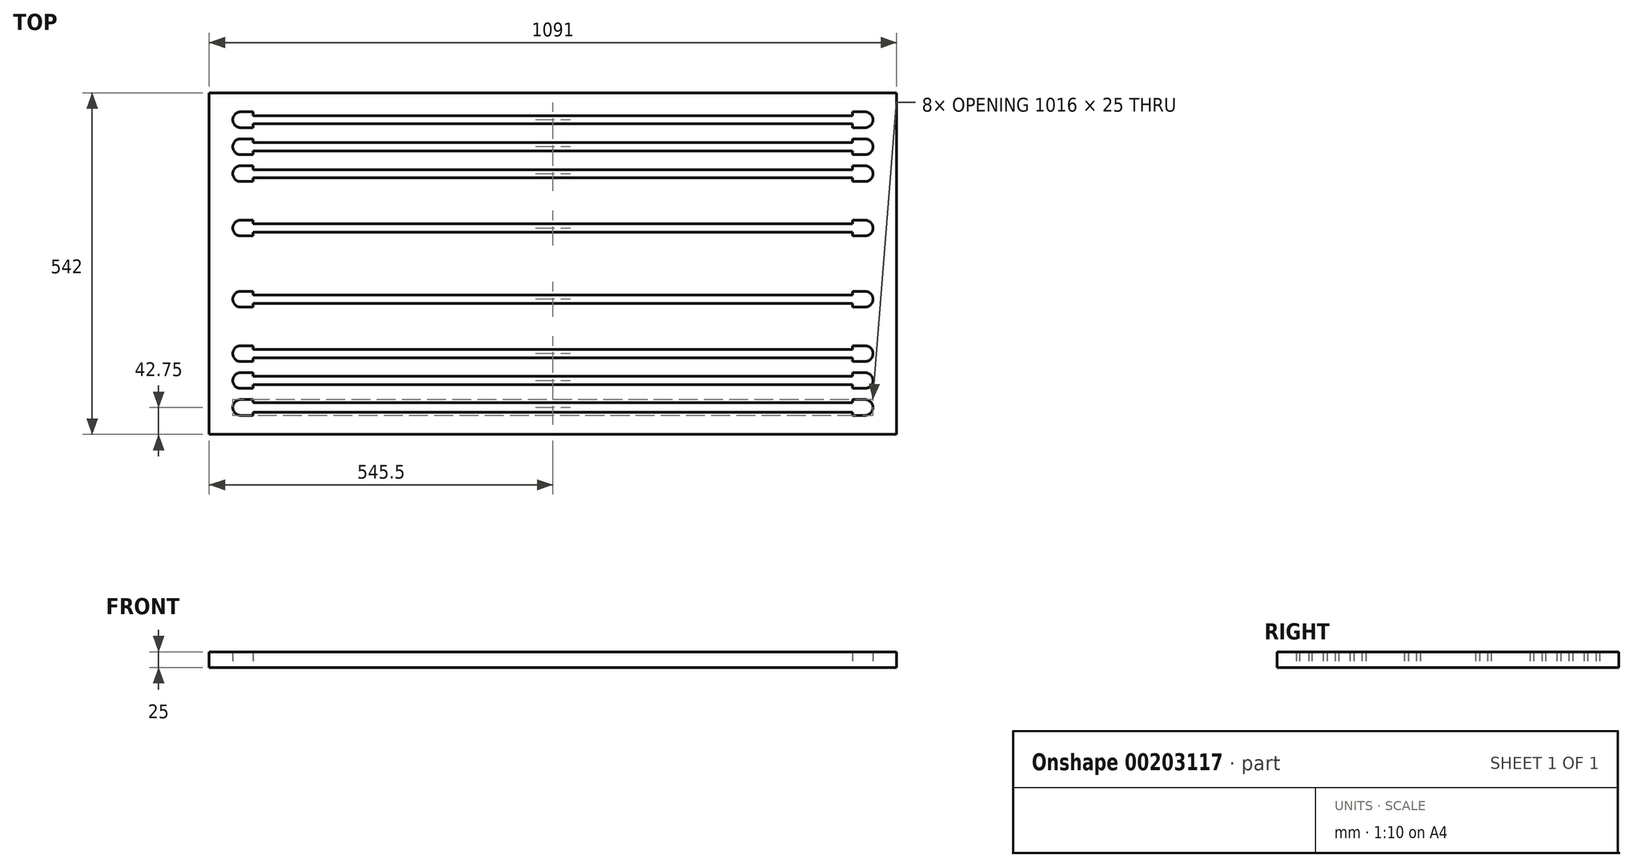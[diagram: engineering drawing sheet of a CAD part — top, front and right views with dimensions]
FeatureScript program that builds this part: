
annotation { "Feature Type Name" : "Feature", "Feature Type Description" : "" }
export const myFeature = defineFeature(function(context is Context, id is Id, definition is map)
    precondition{}
    {
        {
            var Q0;
            Q0=qCreatedBy(makeId("Top.planeOp"),FACE);
            var sketch = newSketch(context, id + "F0", { "sketchPlane" : qUnion([Q0])});
            skLineSegment(sketch, "E0.bottom", {"start": v(0, 0) * mm, "end": v(1091, 0) * mm});
            skLineSegment(sketch, "E0.top", {"start": v(0, 542) * mm, "end": v(1091, 542) * mm});
            skLineSegment(sketch, "E0.left", {"start": v(0, 0) * mm, "end": v(0, 542) * mm});
            skLineSegment(sketch, "E0.right", {"start": v(1091, 0) * mm, "end": v(1091, 542) * mm});
            skPoint(sketch, "E1", {"position": v(214, 171) * mm});
            skPoint(sketch, "E2", {"position": v(214, 271) * mm});
            skPoint(sketch, "E3", {"position": v(214, 371) * mm});
            skLineSegment(sketch, "E4", {"start": v(-315.3, 371) * mm, "end": v(-315.3, 271) * mm, "construction": true});
            skLineSegment(sketch, "E5", {"start": v(-315.3, 271) * mm, "end": v(-315.3, 171) * mm, "construction": true});
            skLineSegment(sketch, "E6", {"start": v(-315.3, 171) * mm, "end": v(-315.3, 0) * mm, "construction": true});
            skLineSegment(sketch, "E7", {"start": v(-315.3, 542) * mm, "end": v(-315.3, 371) * mm, "construction": true});
            skPoint(sketch, "E8", {"position": v(-315.3, 456.5) * mm});
            skPoint(sketch, "E9", {"position": v(-315.3, 327.44) * mm});
            skPoint(sketch, "E10", {"position": v(-315.3, 221) * mm});
            skPoint(sketch, "E11", {"position": v(-315.3, 85.5) * mm});
            skLineSegment(sketch, "E12", {"start": v(50, 327.44) * mm, "end": v(1041, 327.44) * mm, "construction": true});
            skLineSegment(sketch, "E13", {"start": v(50, 456.5) * mm, "end": v(1041, 456.5) * mm, "construction": true});
            skLineSegment(sketch, "E14", {"start": v(1046.67, 271) * mm, "end": v(1429.51, 271) * mm, "construction": true});
            skPoint(sketch, "E14.endSnap0", {"position": v(1091, 271) * mm});
            skLineSegment(sketch, "E15", {"start": v(-218.04, 542) * mm, "end": v(-218.04, 456.5) * mm, "construction": true});
            skPoint(sketch, "E16", {"position": v(-218.04, 499.25) * mm});
            skLineSegment(sketch, "E17", {"start": v(50, 499.25) * mm, "end": v(1041, 499.25) * mm, "construction": true});
            skLineSegment(sketch, "E18", {"start": v(-218.04, 456.5) * mm, "end": v(-218.04, 371) * mm, "construction": true});
            skPoint(sketch, "E19", {"position": v(-218.04, 413.75) * mm});
            skLineSegment(sketch, "E20", {"start": v(50, 413.75) * mm, "end": v(1041, 413.75) * mm, "construction": true});
            skLineSegment(sketch, "E21.MirrorCS", {"start": v(50, 42.75) * mm, "end": v(1041, 42.75) * mm, "construction": true});
            skLineSegment(sketch, "E22.MirrorCS", {"start": v(50, 85.5) * mm, "end": v(1041, 85.5) * mm, "construction": true});
            skLineSegment(sketch, "E23.MirrorCS", {"start": v(50, 128.25) * mm, "end": v(1041, 128.25) * mm, "construction": true});
            skLineSegment(sketch, "E24.MirrorCS", {"start": v(50, 214.56) * mm, "end": v(1041, 214.56) * mm, "construction": true});
            skSolve(sketch);
        }
        {
            var Q0;
            Q0=makeQuery(id+"F0.imprint","IMPRINT",FACE,{"disambiguationData":[TD([[makeQuery(id+"F0.imprint","IMPRINT",EDGE,{"derivedFrom":sQuery(id+"F0.wireOp",EDGE,"E0.bottom")}),1.0]])]});
            var sketch = newSketch(context, id + "F1", { "sketchPlane" : qUnion([Q0])});
            skLineSegment(sketch, "E25.bottom", {"start": v(0, 0) * mm, "end": v(1091, 0) * mm});
            skLineSegment(sketch, "E25.top", {"start": v(0, 542) * mm, "end": v(1091, 542) * mm});
            skLineSegment(sketch, "E25.left", {"start": v(0, 0) * mm, "end": v(0, 542) * mm});
            skLineSegment(sketch, "E25.right", {"start": v(1091, 0) * mm, "end": v(1091, 542) * mm});
            skLineSegment(sketch, "E26.JFx.JFx", {"start": v(50, 499.25) * mm, "end": v(1041, 499.25) * mm, "construction": true});
            skLineSegment(sketch, "E26.JFl.JFl", {"start": v(50, 456.5) * mm, "end": v(1041, 456.5) * mm, "construction": true});
            skLineSegment(sketch, "E26.JF5.JF5", {"start": v(50, 413.75) * mm, "end": v(1041, 413.75) * mm, "construction": true});
            skLineSegment(sketch, "E26.JFh.JFh", {"start": v(50, 327.44) * mm, "end": v(1041, 327.44) * mm, "construction": true});
            skLineSegment(sketch, "E26.KFJB.KFJB", {"start": v(50, 214.56) * mm, "end": v(1041, 214.56) * mm, "construction": true});
            skLineSegment(sketch, "E26.KFFB.KFFB", {"start": v(50, 128.25) * mm, "end": v(1041, 128.25) * mm, "construction": true});
            skLineSegment(sketch, "E26.KFBB.KFBB", {"start": v(50, 85.5) * mm, "end": v(1041, 85.5) * mm, "construction": true});
            skLineSegment(sketch, "E26.JF9.JF9", {"start": v(50, 42.75) * mm, "end": v(1041, 42.75) * mm, "construction": true});
            skArc(sketch, "E26.0.startCap", {"start": v(50, 486.75) * mm, "mid": v(37.5, 499.25) * mm, "end": v(50, 511.75) * mm});
            skArc(sketch, "E26.0.endCap", {"start": v(1041, 511.75) * mm, "mid": v(1053.5, 499.25) * mm, "end": v(1041, 486.75) * mm});
            skLineSegment(sketch, "E26.0.left", {"start": v(50, 511.75) * mm, "end": v(70, 511.75) * mm});
            skLineSegment(sketch, "E26.0.right", {"start": v(50, 486.75) * mm, "end": v(70, 486.75) * mm});
            skArc(sketch, "E26.1.startCap", {"start": v(50, 444) * mm, "mid": v(37.5, 456.5) * mm, "end": v(50, 469) * mm});
            skArc(sketch, "E26.1.endCap", {"start": v(1041, 469) * mm, "mid": v(1053.5, 456.5) * mm, "end": v(1041, 444) * mm});
            skLineSegment(sketch, "E26.1.left", {"start": v(50, 469) * mm, "end": v(70, 469) * mm});
            skLineSegment(sketch, "E26.1.right", {"start": v(50, 444) * mm, "end": v(70, 444) * mm});
            skArc(sketch, "E26.2.startCap", {"start": v(50, 401.25) * mm, "mid": v(37.5, 413.75) * mm, "end": v(50, 426.25) * mm});
            skArc(sketch, "E26.2.endCap", {"start": v(1041, 426.25) * mm, "mid": v(1053.5, 413.75) * mm, "end": v(1041, 401.25) * mm});
            skLineSegment(sketch, "E26.2.left", {"start": v(50, 426.25) * mm, "end": v(70, 426.25) * mm});
            skLineSegment(sketch, "E26.2.right", {"start": v(50, 401.25) * mm, "end": v(70, 401.25) * mm});
            skArc(sketch, "E26.3.startCap", {"start": v(50, 314.94) * mm, "mid": v(37.5, 327.44) * mm, "end": v(50, 339.94) * mm});
            skArc(sketch, "E26.3.endCap", {"start": v(1041, 339.94) * mm, "mid": v(1053.5, 327.44) * mm, "end": v(1041, 314.94) * mm});
            skLineSegment(sketch, "E26.3.left", {"start": v(50, 339.94) * mm, "end": v(70, 339.94) * mm});
            skLineSegment(sketch, "E26.3.right", {"start": v(50, 314.94) * mm, "end": v(70, 314.94) * mm});
            skArc(sketch, "E26.4.startCap", {"start": v(50, 202.06) * mm, "mid": v(37.5, 214.56) * mm, "end": v(50, 227.06) * mm});
            skArc(sketch, "E26.4.endCap", {"start": v(1041, 227.06) * mm, "mid": v(1053.5, 214.56) * mm, "end": v(1041, 202.06) * mm});
            skLineSegment(sketch, "E26.4.right", {"start": v(50, 202.06) * mm, "end": v(70, 202.06) * mm});
            skArc(sketch, "E26.5.startCap", {"start": v(50, 115.75) * mm, "mid": v(37.5, 128.25) * mm, "end": v(50, 140.75) * mm});
            skArc(sketch, "E26.5.endCap", {"start": v(1041, 140.75) * mm, "mid": v(1053.5, 128.25) * mm, "end": v(1041, 115.75) * mm});
            skLineSegment(sketch, "E26.5.left", {"start": v(50, 140.75) * mm, "end": v(70, 140.75) * mm});
            skLineSegment(sketch, "E26.5.right", {"start": v(50, 115.75) * mm, "end": v(70, 115.75) * mm});
            skArc(sketch, "E26.6.startCap", {"start": v(50, 73) * mm, "mid": v(37.5, 85.5) * mm, "end": v(50, 98) * mm});
            skArc(sketch, "E26.6.endCap", {"start": v(1041, 98) * mm, "mid": v(1053.5, 85.5) * mm, "end": v(1041, 73) * mm});
            skLineSegment(sketch, "E26.6.left", {"start": v(50, 98) * mm, "end": v(70, 98) * mm});
            skLineSegment(sketch, "E26.6.right", {"start": v(50, 73) * mm, "end": v(70, 73) * mm});
            skArc(sketch, "E26.7.startCap", {"start": v(50, 30.25) * mm, "mid": v(37.5, 42.75) * mm, "end": v(50, 55.25) * mm});
            skArc(sketch, "E26.7.endCap", {"start": v(1041, 55.25) * mm, "mid": v(1053.5, 42.75) * mm, "end": v(1041, 30.25) * mm});
            skLineSegment(sketch, "E26.7.left", {"start": v(50, 55.25) * mm, "end": v(70, 55.25) * mm});
            skLineSegment(sketch, "E26.7.right", {"start": v(50, 30.25) * mm, "end": v(70, 30.25) * mm});
            skPoint(sketch, "E27", {"position": v(545.5, 511.75) * mm});
            skLineSegment(sketch, "E28.top", {"start": v(70, 505.75) * mm, "end": v(1021, 505.75) * mm});
            skLineSegment(sketch, "E28.left", {"start": v(70, 511.75) * mm, "end": v(70, 505.75) * mm});
            skLineSegment(sketch, "E28.right", {"start": v(1021, 511.75) * mm, "end": v(1021, 505.75) * mm});
            skLineSegment(sketch, "E29.bottom", {"start": v(70, 492.75) * mm, "end": v(1021, 492.75) * mm});
            skLineSegment(sketch, "E29.left", {"start": v(70, 492.75) * mm, "end": v(70, 486.75) * mm});
            skLineSegment(sketch, "E29.right", {"start": v(1021, 492.75) * mm, "end": v(1021, 486.75) * mm});
            skLineSegment(sketch, "E30.top", {"start": v(70, 92) * mm, "end": v(1021, 92) * mm});
            skLineSegment(sketch, "E30.left", {"start": v(1021, 98) * mm, "end": v(1021, 92) * mm});
            skLineSegment(sketch, "E30.right", {"start": v(70, 98) * mm, "end": v(70, 92) * mm});
            skPoint(sketch, "E31", {"position": v(545.5, 98) * mm});
            skLineSegment(sketch, "E32.bottom", {"start": v(70, 79) * mm, "end": v(1021, 79) * mm});
            skLineSegment(sketch, "E32.left", {"start": v(1021, 79) * mm, "end": v(1021, 73) * mm});
            skLineSegment(sketch, "E32.right", {"start": v(70, 79) * mm, "end": v(70, 73) * mm});
            skLineSegment(sketch, "E33.top", {"start": v(70, 420.25) * mm, "end": v(1021, 420.25) * mm});
            skLineSegment(sketch, "E33.left", {"start": v(1021, 426.25) * mm, "end": v(1021, 420.25) * mm});
            skLineSegment(sketch, "E33.right", {"start": v(70, 426.25) * mm, "end": v(70, 420.25) * mm});
            skPoint(sketch, "E34", {"position": v(545.5, 426.25) * mm});
            skLineSegment(sketch, "E35.bottom", {"start": v(70, 407.25) * mm, "end": v(1021, 407.25) * mm});
            skLineSegment(sketch, "E35.left", {"start": v(1021, 407.25) * mm, "end": v(1021, 401.25) * mm});
            skLineSegment(sketch, "E35.right", {"start": v(70, 407.25) * mm, "end": v(70, 401.25) * mm});
            skLineSegment(sketch, "E36.top", {"start": v(70, 463) * mm, "end": v(1021, 463) * mm});
            skLineSegment(sketch, "E36.left", {"start": v(1021, 469) * mm, "end": v(1021, 463) * mm});
            skLineSegment(sketch, "E36.right", {"start": v(70, 469) * mm, "end": v(70, 463) * mm});
            skPoint(sketch, "E37", {"position": v(545.5, 469) * mm});
            skLineSegment(sketch, "E38.bottom", {"start": v(70, 450) * mm, "end": v(1021, 450) * mm});
            skLineSegment(sketch, "E38.left", {"start": v(1021, 450) * mm, "end": v(1021, 444) * mm});
            skLineSegment(sketch, "E38.right", {"start": v(70, 450) * mm, "end": v(70, 444) * mm});
            skPoint(sketch, "E39", {"position": v(545.5, 339.94) * mm});
            skPoint(sketch, "E40", {"position": v(545.5, 227.06) * mm});
            skPoint(sketch, "E41", {"position": v(545.5, 140.75) * mm});
            skPoint(sketch, "E42", {"position": v(545.5, 55.25) * mm});
            skLineSegment(sketch, "E43.top", {"start": v(70, 134.75) * mm, "end": v(1021, 134.75) * mm});
            skLineSegment(sketch, "E43.left", {"start": v(70, 140.75) * mm, "end": v(70, 134.75) * mm});
            skLineSegment(sketch, "E43.right", {"start": v(1021, 140.75) * mm, "end": v(1021, 134.75) * mm});
            skLineSegment(sketch, "E44.bottom", {"start": v(70, 121.75) * mm, "end": v(1021, 121.75) * mm});
            skLineSegment(sketch, "E44.left", {"start": v(70, 121.75) * mm, "end": v(70, 115.75) * mm});
            skLineSegment(sketch, "E44.right", {"start": v(1021, 121.75) * mm, "end": v(1021, 115.75) * mm});
            skLineSegment(sketch, "E45.top", {"start": v(70, 50.25) * mm, "end": v(1021, 50.25) * mm});
            skLineSegment(sketch, "E45.left", {"start": v(70, 55.25) * mm, "end": v(70, 50.25) * mm});
            skLineSegment(sketch, "E45.right", {"start": v(1021, 55.25) * mm, "end": v(1021, 50.25) * mm});
            skLineSegment(sketch, "E46.bottom", {"start": v(70, 35.25) * mm, "end": v(1021, 35.25) * mm});
            skLineSegment(sketch, "E46.left", {"start": v(70, 35.25) * mm, "end": v(70, 30.25) * mm});
            skLineSegment(sketch, "E46.right", {"start": v(1021, 35.25) * mm, "end": v(1021, 30.25) * mm});
            skLineSegment(sketch, "E47.top", {"start": v(70, 221.06) * mm, "end": v(1021, 221.06) * mm});
            skLineSegment(sketch, "E47.left", {"start": v(70, 227.06) * mm, "end": v(70, 221.06) * mm});
            skLineSegment(sketch, "E47.right", {"start": v(1021, 227.06) * mm, "end": v(1021, 221.06) * mm});
            skLineSegment(sketch, "E48.bottom", {"start": v(70, 208.06) * mm, "end": v(1021, 208.06) * mm});
            skLineSegment(sketch, "E48.left", {"start": v(70, 208.06) * mm, "end": v(70, 202.06) * mm});
            skLineSegment(sketch, "E48.right", {"start": v(1021, 208.06) * mm, "end": v(1021, 202.06) * mm});
            skPoint(sketch, "E49", {"position": v(545.5, 30.25) * mm});
            skLineSegment(sketch, "E50.top", {"start": v(70, 333.94) * mm, "end": v(1021, 333.94) * mm});
            skLineSegment(sketch, "E50.left", {"start": v(70, 339.94) * mm, "end": v(70, 333.94) * mm});
            skLineSegment(sketch, "E50.right", {"start": v(1021, 339.94) * mm, "end": v(1021, 333.94) * mm});
            skLineSegment(sketch, "E51.bottom", {"start": v(70, 320.94) * mm, "end": v(1021, 320.94) * mm});
            skLineSegment(sketch, "E51.left", {"start": v(70, 320.94) * mm, "end": v(70, 314.94) * mm});
            skLineSegment(sketch, "E51.right", {"start": v(1021, 320.94) * mm, "end": v(1021, 314.94) * mm});
            skPoint(sketch, "E52", {"position": v(545.5, 214.56) * mm});
            skLineSegment(sketch, "E53.trimOffspring", {"start": v(1021, 140.75) * mm, "end": v(1041, 140.75) * mm});
            skLineSegment(sketch, "E54.trimOffspring", {"start": v(1021, 98) * mm, "end": v(1041, 98) * mm});
            skLineSegment(sketch, "E55.trimOffspring", {"start": v(1021, 55.25) * mm, "end": v(1041, 55.25) * mm});
            skLineSegment(sketch, "E56.trimOffspring", {"start": v(1021, 73) * mm, "end": v(1041, 73) * mm});
            skLineSegment(sketch, "E57.trimOffspring", {"start": v(1021, 30.25) * mm, "end": v(1041, 30.25) * mm});
            skLineSegment(sketch, "E58.trimOffspring", {"start": v(1021, 115.75) * mm, "end": v(1041, 115.75) * mm});
            skLineSegment(sketch, "E59.trimOffspring", {"start": v(1021, 202.06) * mm, "end": v(1041, 202.06) * mm});
            skLineSegment(sketch, "E60.trimOffspring", {"start": v(1021, 227.06) * mm, "end": v(1041, 227.06) * mm});
            skLineSegment(sketch, "E61.trimOffspring", {"start": v(1021, 339.94) * mm, "end": v(1041, 339.94) * mm});
            skLineSegment(sketch, "E62.trimOffspring", {"start": v(1021, 314.94) * mm, "end": v(1041, 314.94) * mm});
            skLineSegment(sketch, "E63.trimOffspring", {"start": v(1021, 401.25) * mm, "end": v(1041, 401.25) * mm});
            skLineSegment(sketch, "E64.trimOffspring", {"start": v(1021, 426.25) * mm, "end": v(1041, 426.25) * mm});
            skLineSegment(sketch, "E65.trimOffspring", {"start": v(1021, 444) * mm, "end": v(1041, 444) * mm});
            skLineSegment(sketch, "E66.trimOffspring", {"start": v(1021, 469) * mm, "end": v(1041, 469) * mm});
            skLineSegment(sketch, "E67.trimOffspring", {"start": v(1021, 486.75) * mm, "end": v(1041, 486.75) * mm});
            skLineSegment(sketch, "E68.trimOffspring", {"start": v(1021, 511.75) * mm, "end": v(1041, 511.75) * mm});
            skLineSegment(sketch, "E69.MirrorCS", {"start": v(50, 227.06) * mm, "end": v(70, 227.06) * mm});
            skSolve(sketch);
        }
        {
            var Q0;
            Q0=makeQuery(id+"F1.imprint","IMPRINT",FACE,{"disambiguationData":[TD([[makeQuery(id+"F1.imprint","IMPRINT",EDGE,{"derivedFrom":sQuery(id+"F1.wireOp",EDGE,"E25.bottom")}),1.0]])]});
            extrude(context, id + "F2", {"entities" : qUnion([Q0]), "depth" : 25 * mm});
        }
    });
